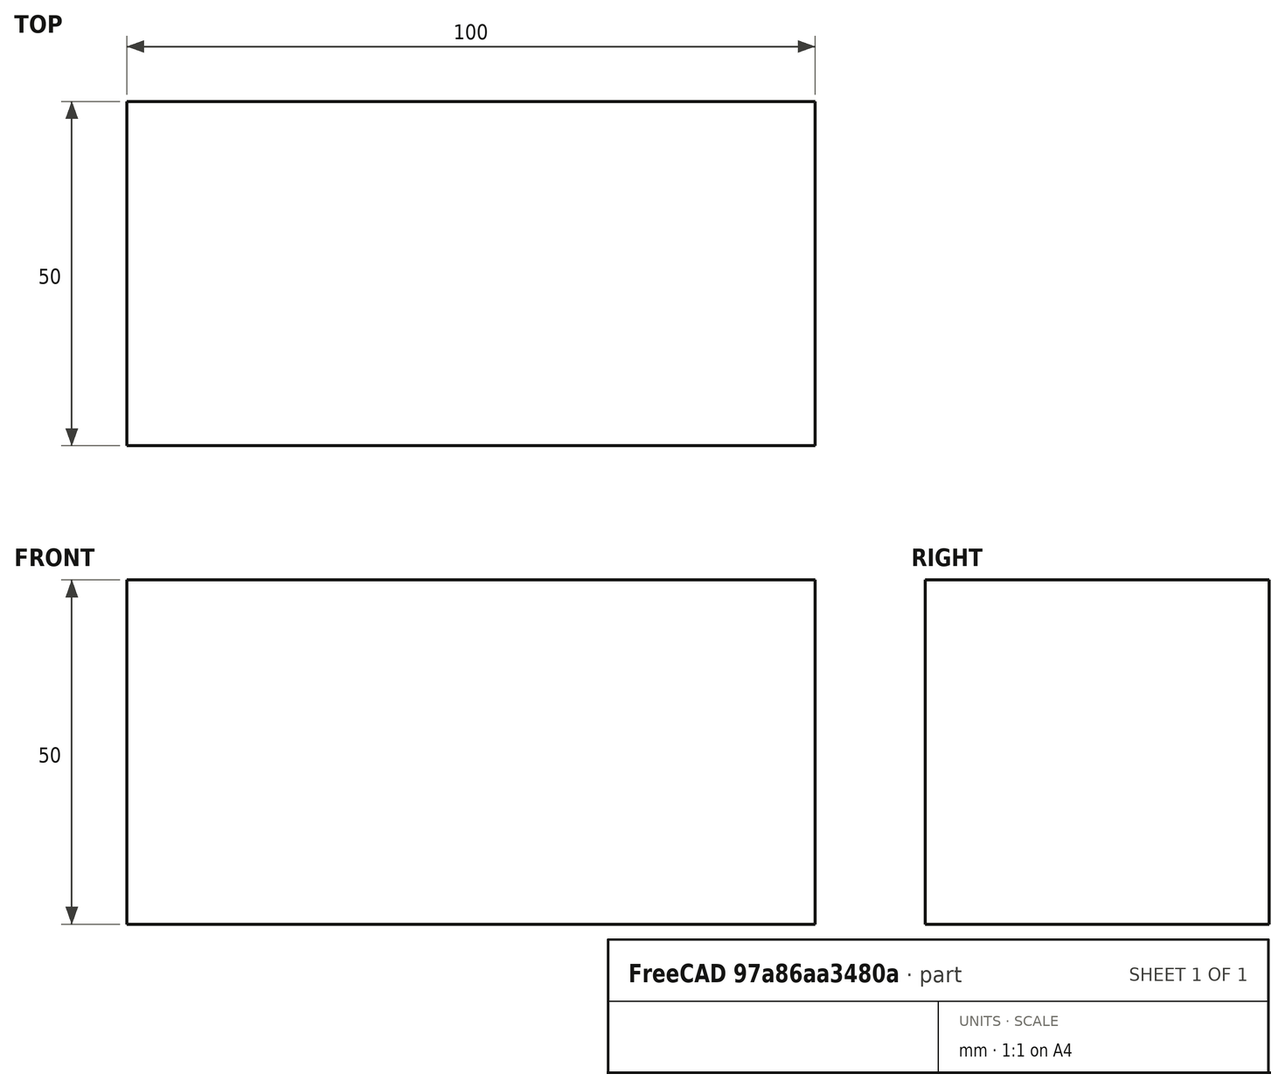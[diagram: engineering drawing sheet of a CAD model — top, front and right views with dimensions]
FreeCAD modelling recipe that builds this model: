
FCSTD DOCUMENT  (FreeCAD 0.15R4671 (Git))
Label: Flat Bar 100x50 EN10058 S235JR
License: All rights reserved
LicenseURL: http://en.wikipedia.org/wiki/All_rights_reserved
objects: Sketcher::SketchObject×1, Part::Extrusion×1
note: 2 computed .brp shape members not serialized (recipe doc carries the construction recipe); baked Part::Feature solids carry a one-line shape summary decoded from their .brp

FEATURE [Sketcher::SketchObject] Sketch
  sketch-geometry (4):
    g0: LineSegment StartX=-50 StartY=-25 StartZ=0 EndX=50 EndY=-25 EndZ=0
    g1: LineSegment StartX=50 StartY=-25 StartZ=0 EndX=50 EndY=25 EndZ=0
    g2: LineSegment StartX=50 StartY=25 StartZ=0 EndX=-50 EndY=25 EndZ=0
    g3: LineSegment StartX=-50 StartY=25 StartZ=0 EndX=-50 EndY=-25 EndZ=0
  constraints (12):
    c: Coincident(g0,g1)
    c: Coincident(g1,g2)
    c: Coincident(g2,g3)
    c: Coincident(g3,g0)
    c: Horizontal(g0)
    c: Horizontal(g2)
    c: Vertical(g1)
    c: Vertical(g3)
    c: Symmetric(g1,g2,g-2)
    c: Symmetric(g0,g1,g-1)
    c: DistanceY(g1) = 50
    c: DistanceX(g0) = 100
FEATURE [Part::Extrusion] Extrude  label="Flat Bar 100x50 EN10058 S235JR"
  Base = -> Sketch
  Dir = (0,0,50)
  Solid = true
